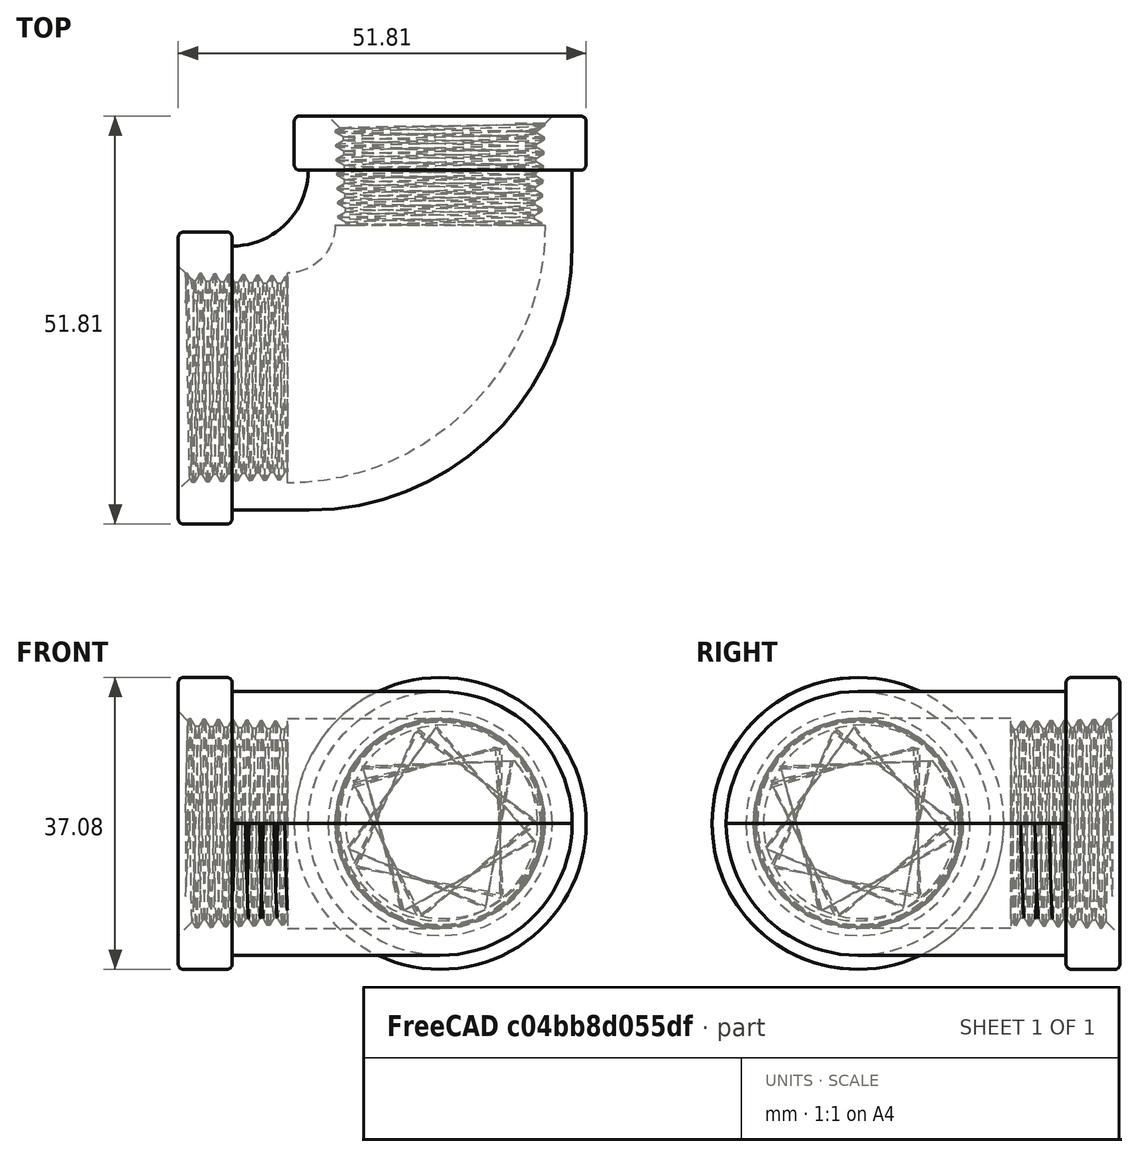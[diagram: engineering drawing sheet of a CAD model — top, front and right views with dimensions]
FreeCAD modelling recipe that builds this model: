
FCSTD DOCUMENT  (FreeCAD 0.16R6712 (Git))
Label: 0.75 NPT elbow from STEP
License: All rights reserved
LicenseURL: http://en.wikipedia.org/wiki/All_rights_reserved
objects: Part::Feature×2, Part::Box×1, Part::Cut×1, App::MeasureDistance×1
note: 4 computed .brp shape members not serialized (recipe doc carries the construction recipe); baked Part::Feature solids carry a one-line shape summary decoded from their .brp

FEATURE [Part::Feature] Part__Feature  label="44605K115"
  shape: bbox 53.34 x 53.34 x 40.14 mm, 66 faces (baked)
FEATURE [Part::Box] Box  label="Cube"
  Height = 50.8
  Length = 50.8
  Placement = pos=(-25.4,25.4,-25.4) rot=(0,0,1;0rad)
  Width = 10
FEATURE [Part::Feature] Part__Feature001  label="44605K116"
  shape: bbox 53.34 x 53.34 x 40.14 mm, 66 faces (baked)
FEATURE [Part::Cut] Cut
  Base = -> Part__Feature001
  Tool = -> Box
FEATURE [App::MeasureDistance] Distance  label="Distance: 0.938544 in"
  Distance = 23.839
  P1 = (-20.6594,11.896,0.0462588)
  P2 = (-19.7552,-11.9259,0.0543012)
